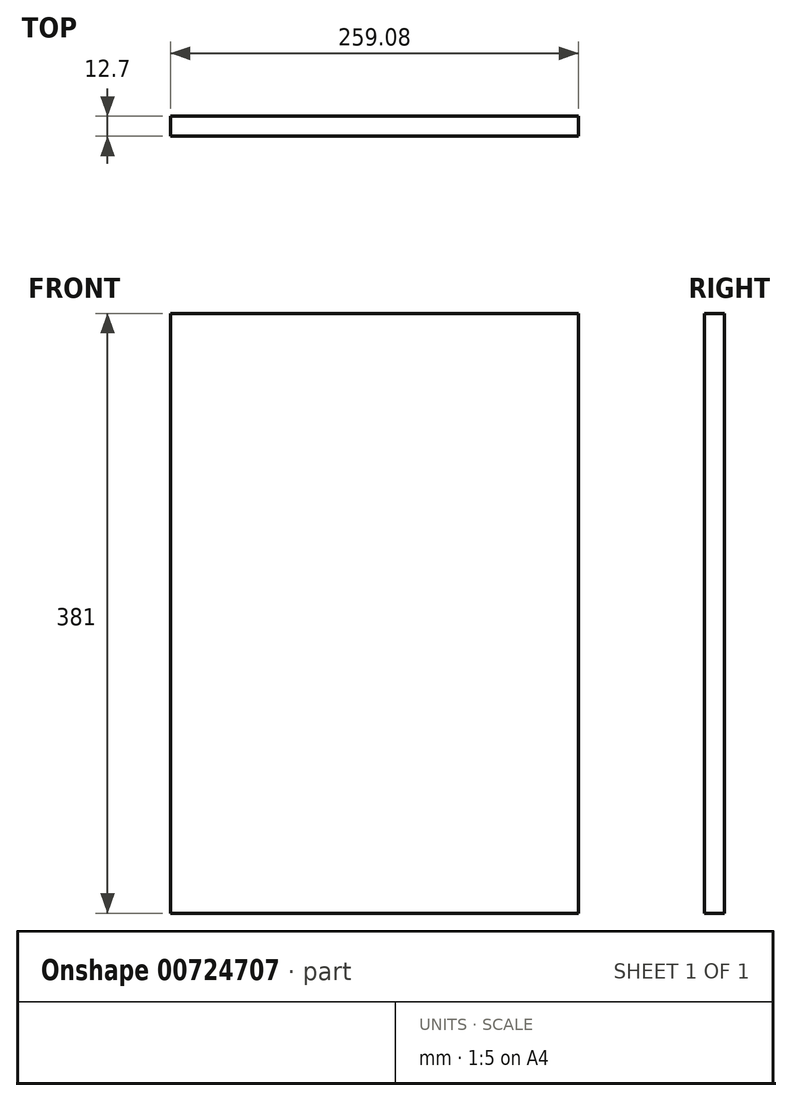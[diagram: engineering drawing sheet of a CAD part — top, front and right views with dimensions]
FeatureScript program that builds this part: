
annotation { "Feature Type Name" : "Feature", "Feature Type Description" : "" }
export const myFeature = defineFeature(function(context is Context, id is Id, definition is map)
    precondition{}
    {
        {
            var Q0;
            Q0=qCreatedBy(makeId("Front.planeOp"),FACE);
            var sketch = newSketch(context, id + "F0", { "sketchPlane" : qUnion([Q0])});
            skLineSegment(sketch, "E0.bottom", {"start": v(-134.1, 281.67) * mm, "end": v(124.98, 281.67) * mm});
            skLineSegment(sketch, "E0.top", {"start": v(-134.1, -99.33) * mm, "end": v(124.98, -99.33) * mm});
            skLineSegment(sketch, "E0.left", {"start": v(-134.1, 281.67) * mm, "end": v(-134.1, -99.33) * mm});
            skLineSegment(sketch, "E0.right", {"start": v(124.98, 281.67) * mm, "end": v(124.98, -99.33) * mm});
            skSolve(sketch);
        }
        {
            var Q0;
            Q0=makeQuery(id+"F0.imprint","IMPRINT",FACE,{"disambiguationData":[TD([[makeQuery(id+"F0.imprint","IMPRINT",EDGE,{"derivedFrom":sQuery(id+"F0.wireOp",EDGE,"E0.bottom")}),-1.0]])]});
            extrude(context, id + "F1", {"entities" : qUnion([Q0]), "depth" : 12.7 * mm, "offsetDistance" : 25.4 * mm});
        }
    });
